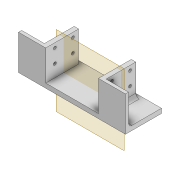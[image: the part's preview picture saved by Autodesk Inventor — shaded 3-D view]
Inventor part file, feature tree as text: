
AUTODESK INVENTOR PART (.ipt)
format: ipt  version: 2022 (Build 260153000, 153)  size: 206,336 bytes
history: native  units: mm
features: extrude x6, sketch x6, projected_geometry x3, plane x1, fillet x1
ambient origin geometry x8: Origin, YZ Plane, XZ Plane, XY Plane, X Axis, Y Axis, Z Axis, Center Point
bodies: Solid1 (feature_tree)
feature tree (17):
  extrude  "Extrusion1"  Depth=20.4mm
  extrude  "Extrusion11"  Depth=54.8mm TaperAngle=0.0deg
  extrude  "Extrusion12"  Depth=3.0mm
  plane  "Work Plane1"
  extrude  "Extrusion13"  Depth=3.0mm
  extrude  "Extrusion14"  Depth=4.0mm
  fillet  "Fillet5"  Radius=4.0mm
  extrude  "Extrusion15"  Depth=27.0mm TaperAngle=0.0deg
  sketch  "Sketch2"  dims[d5=20.4mm d6=20.4mm]
  sketch  "Sketch13"  dims[d8=6.0mm d9=54.8mm d10=0.0mm]
  sketch  "Sketch14"  dims[d22=4.0mm d23=3.0mm]
  sketch  "Sketch15"  dims[d24=3.0mm d27=8.0mm]
  projected_geometry  "Projected Loop12"
  sketch  "Sketch16"  dims[d28=8.0mm d75=4.0mm d76=4.0mm]
  projected_geometry  "Projected Loop13"
  projected_geometry  "Projected Loop14"
  sketch  "Sketch17"  dims[d77=46.8mm d78=27.0mm d79=0.0mm d80=2.6mm d82=2.6mm d86=2.6mm d87=2.6mm d92=100.0mm d93=0.0mm d95=16.0mm d96=16.0mm d97=5.2mm d98=5.2mm d99=5.2mm d100=5.2mm d101=11.0mm d102=23.0mm d103=32.0mm d104=20.0mm d105=75.0mm d106=0.0mm d107=0.0mm d108=27.0mm d109=0.0mm d110=3.0mm d111=100.0mm d112=0.0mm]
